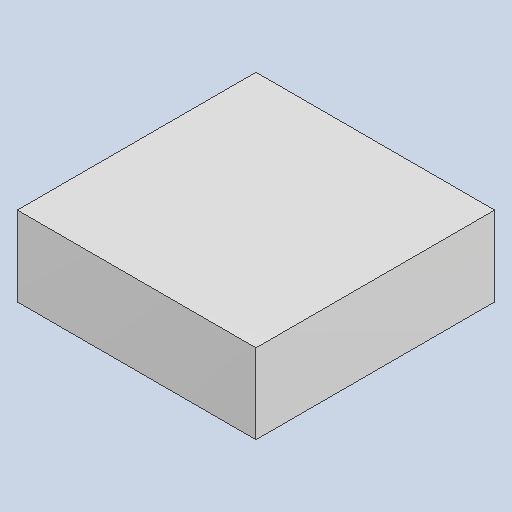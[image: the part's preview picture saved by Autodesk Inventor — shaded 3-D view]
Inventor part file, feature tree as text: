
AUTODESK INVENTOR PART (.ipt)
format: ipt  version: 2023.4 (Build 274418000, 418)  size: 79,872 bytes
history: native  units: mm
features: extrude x1
ambient origin geometry x8: Origin, YZ Plane, XZ Plane, XY Plane, X Axis, Y Axis, Z Axis, Center Point
bodies: Solid1 (feature_tree)
feature tree (1):
  extrude  "Extruded_28"  [1 undecoded]
note: 1 required parameter value undecoded (feature->parameter linkage not recoverable at this tier; creation-order binding heuristic only, values carry confidence <= 0.55)
